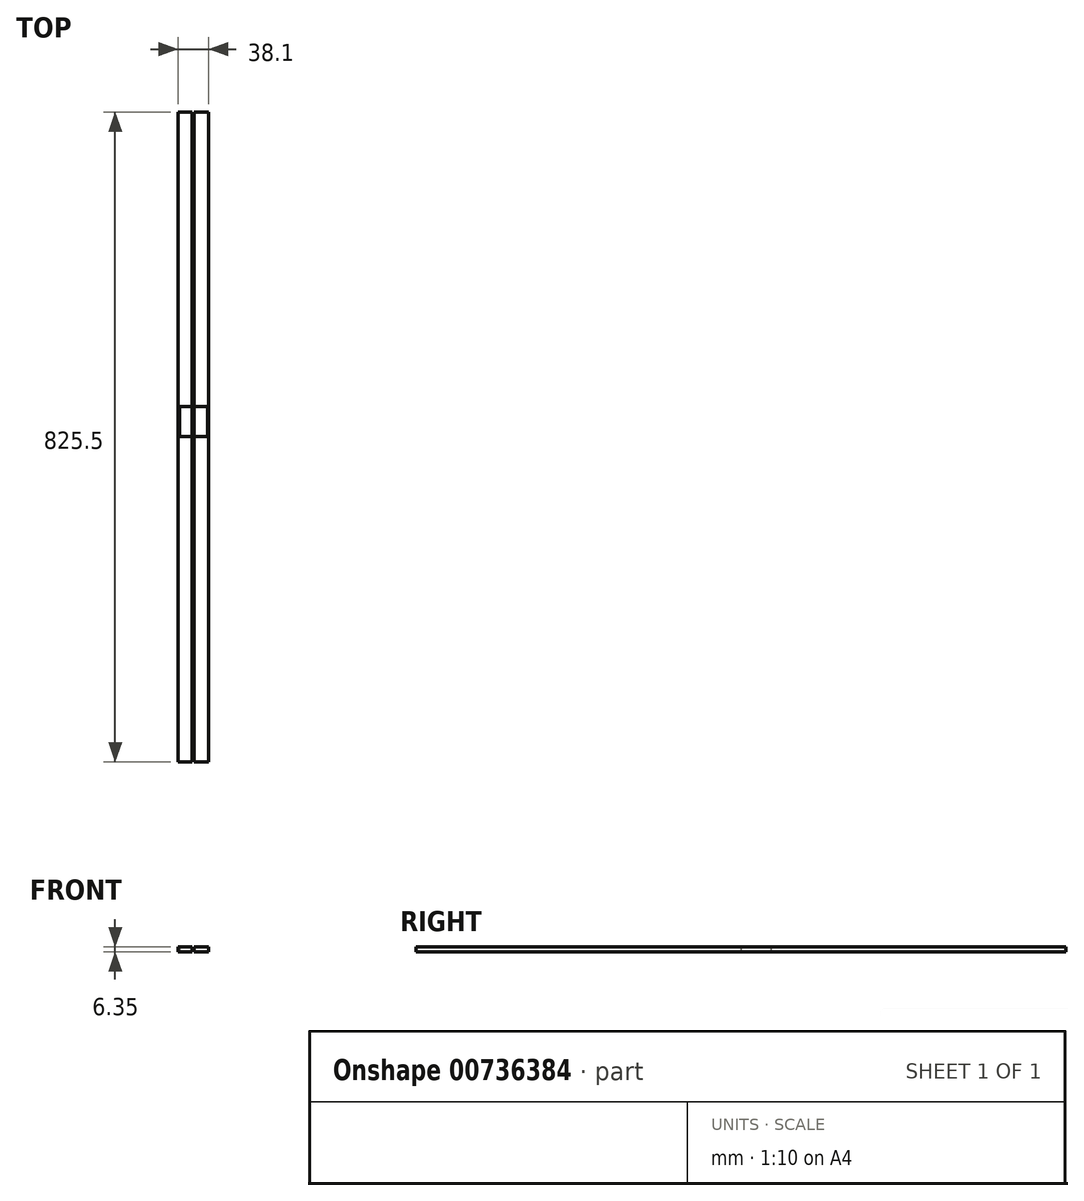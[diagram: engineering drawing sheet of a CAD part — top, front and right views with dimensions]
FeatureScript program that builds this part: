
annotation { "Feature Type Name" : "Feature", "Feature Type Description" : "" }
export const myFeature = defineFeature(function(context is Context, id is Id, definition is map)
    precondition{}
    {
        {
            var Q0;
            Q0=qCreatedBy(makeId("Top.planeOp"),FACE);
            var sketch = newSketch(context, id + "F0", { "sketchPlane" : qUnion([Q0])});
            skLineSegment(sketch, "E0.bottom", {"start": v(-181.93, 412.2) * mm, "end": v(-143.83, 412.2) * mm});
            skLineSegment(sketch, "E0.top", {"start": v(-181.93, -413.3) * mm, "end": v(-143.83, -413.3) * mm});
            skLineSegment(sketch, "E0.left", {"start": v(-181.93, 412.2) * mm, "end": v(-181.93, -413.3) * mm});
            skLineSegment(sketch, "E0.right", {"start": v(-143.83, 412.2) * mm, "end": v(-143.83, -413.3) * mm});
            skSolve(sketch);
        }
        {
            var Q0;
            Q0=makeQuery(id+"F0.imprint","IMPRINT",FACE,{"disambiguationData":[TD([[makeQuery(id+"F0.imprint","IMPRINT",EDGE,{"derivedFrom":sQuery(id+"F0.wireOp",EDGE,"E0.bottom")}),-1.0]])]});
            var sketch = newSketch(context, id + "F1", { "sketchPlane" : qUnion([Q0])});
            skLineSegment(sketch, "E1.bottom", {"start": v(-162.06, -555.67) * mm, "end": v(-164.6, -555.67) * mm});
            skLineSegment(sketch, "E1.top", {"start": v(-162.06, 434.93) * mm, "end": v(-164.6, 434.93) * mm});
            skLineSegment(sketch, "E1.left", {"start": v(-162.06, -555.67) * mm, "end": v(-162.06, 434.93) * mm});
            skLineSegment(sketch, "E1.right", {"start": v(-164.6, -555.67) * mm, "end": v(-164.6, 434.93) * mm});
            skSolve(sketch);
        }
        {
            var Q0;
            Q0 = qSketchRegion(id + "F0", true);
            extrude(context, id + "F2", {"entities" : qUnion([Q0]), "depth" : 6.35 * mm, "offsetDistance" : 25.4 * mm});
        }
        {
            var Q0;
            Q0 = qSketchRegion(id + "F1", true);
            extrude(context, id + "F3", {"entities" : qUnion([Q0]), "operationType" : NewBodyOperationType.REMOVE, "depth" : 284.48 * mm, "offsetDistance" : 25.4 * mm});
        }
        {
            var Q0;
            Q0=makeQuery(id+"F0.imprint","IMPRINT",FACE,{"disambiguationData":[TD([[makeQuery(id+"F0.imprint","IMPRINT",EDGE,{"derivedFrom":sQuery(id+"F0.wireOp",EDGE,"E0.bottom")}),-1.0]])]});
            var sketch = newSketch(context, id + "F4", { "sketchPlane" : qUnion([Q0])});
            skLineSegment(sketch, "E2.bottom", {"start": v(-180.14, 38.1) * mm, "end": v(-144.89, 38.1) * mm});
            skLineSegment(sketch, "E2.top", {"start": v(-180.14, 0) * mm, "end": v(-144.89, 0) * mm});
            skLineSegment(sketch, "E2.left", {"start": v(-180.14, 38.1) * mm, "end": v(-180.14, 0) * mm});
            skLineSegment(sketch, "E2.right", {"start": v(-144.89, 38.1) * mm, "end": v(-144.89, 0) * mm});
            skSolve(sketch);
        }
        {
            var Q0;
            {var subQ0=sQuery(id+"F4.wireOp",EDGE,"E2.bottom");var subQ1=makeQuery(id+"F0.imprint","IMPRINT",EDGE,{"derivedFrom":sQuery(id+"F0.wireOp",EDGE,"E0.left")});var subQ2=makeQuery(id+"F4.imprint","INTERSECT",VERTEX,{"derivedFrom":[subQ1,subQ0]});Q0=makeQuery(id+"F4.imprint","IMPRINT",FACE,{"disambiguationData":[TD([[makeQuery(id+"F4.imprint","IMPRINT",EDGE,{"disambiguationData":[TD([[subQ2,-1.0]])],"derivedFrom":subQ0}),-1.0]])]});}
            extrude(context, id + "F5", {"entities" : qUnion([Q0]), "depth" : 6.35 * mm, "offsetDistance" : 25.4 * mm});
        }
        {
            var Q0;
            Q0 = qSketchRegion(id + "F1", true);
            extrude(context, id + "F6", {"entities" : qUnion([Q0]), "operationType" : NewBodyOperationType.REMOVE, "depth" : 33.02 * mm, "offsetDistance" : 25.4 * mm});
        }
    });
